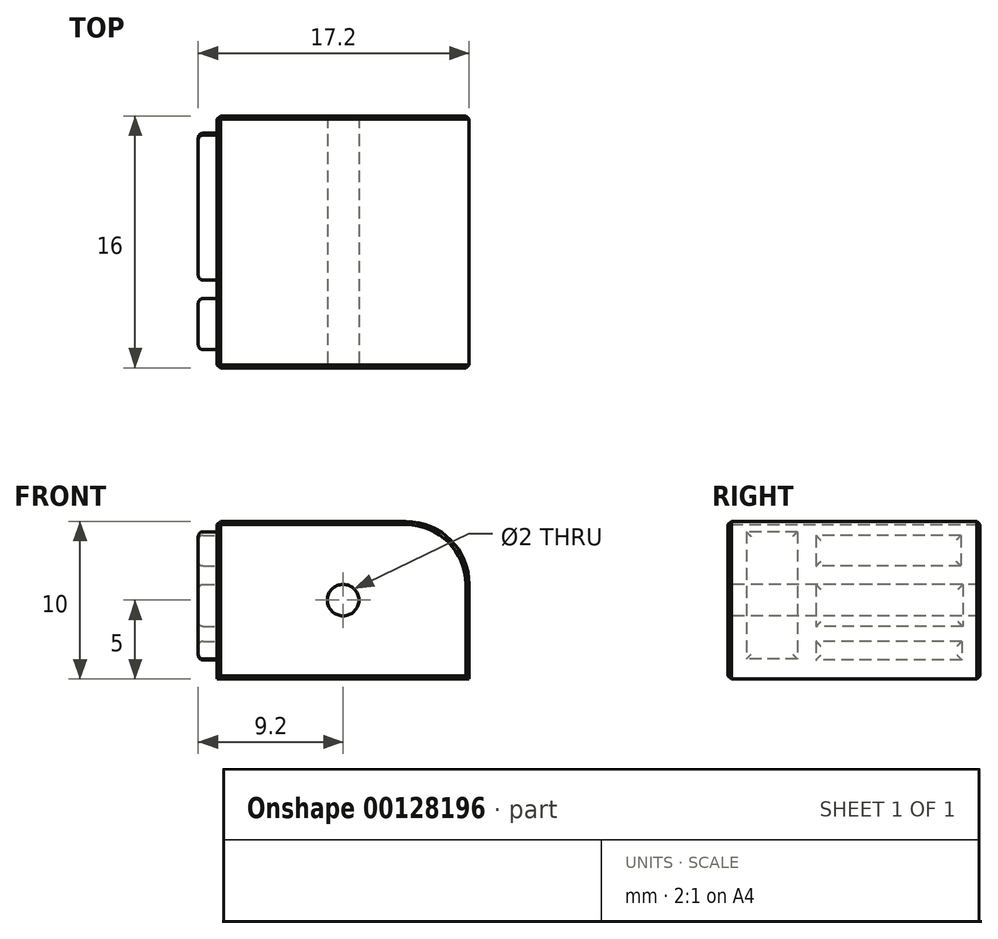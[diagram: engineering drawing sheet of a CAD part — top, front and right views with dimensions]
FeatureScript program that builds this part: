
annotation { "Feature Type Name" : "Feature", "Feature Type Description" : "" }
export const myFeature = defineFeature(function(context is Context, id is Id, definition is map)
    precondition{}
    {
        {
            var Q0;
            Q0=qCreatedBy(makeId("Top.planeOp"),FACE);
            var sketch = newSketch(context, id + "F0", { "sketchPlane" : qUnion([Q0])});
            skLineSegment(sketch, "E0.bottom", {"start": v(8, -8) * mm, "end": v(-8, -8) * mm});
            skLineSegment(sketch, "E0.top", {"start": v(8, 8) * mm, "end": v(-8, 8) * mm});
            skLineSegment(sketch, "E0.left", {"start": v(8, -8) * mm, "end": v(8, 8) * mm});
            skLineSegment(sketch, "E0.right", {"start": v(-8, -8) * mm, "end": v(-8, 8) * mm});
            skPoint(sketch, "E0.middle", {"position": v(0, 0) * mm});
            skSolve(sketch);
        }
        {
            var Q0;
            Q0=makeQuery(id+"F0.imprint","IMPRINT",FACE,{"disambiguationData":[TD([[makeQuery(id+"F0.imprint","IMPRINT",EDGE,{"derivedFrom":sQuery(id+"F0.wireOp",EDGE,"E0.bottom")}),-1.0]])]});
            extrude(context, id + "F1", {"entities" : qUnion([Q0]), "depth" : 10 * mm});
        }
        {
            var Q0;
            Q0=makeQuery(id+"F1.opExtrude","CAP_EDGE",EDGE,{"disambiguationData":[OSD([sQuery(id+"F0.wireOp",EDGE,"E0.left")])],"isStart":false});
            fillet(context, id + "F2", {"entities" : qUnion([Q0]), "radius" : 4 * mm, "tangentPropagation" : true, "allowEdgeOverflow" : false});
        }
        {
            var Q0;
            Q0=makeQuery(id+"F1.opExtrude","SWEPT_FACE",FACE,{"disambiguationData":[OSD([sQuery(id+"F0.wireOp",EDGE,"E0.right")])]});
            var sketch = newSketch(context, id + "F3", { "sketchPlane" : qUnion([Q0])});
            skLineSegment(sketch, "E1.bottom", {"start": v(-6.79, 9.1) * mm, "end": v(2.41, 9.1) * mm});
            skLineSegment(sketch, "E1.top", {"start": v(-6.79, 7.16) * mm, "end": v(2.41, 7.16) * mm});
            skLineSegment(sketch, "E1.left", {"start": v(-6.79, 9.1) * mm, "end": v(-6.79, 7.16) * mm});
            skLineSegment(sketch, "E1.right", {"start": v(2.41, 9.1) * mm, "end": v(2.41, 7.16) * mm});
            skLineSegment(sketch, "E2.bottom", {"start": v(-6.9, 5.98) * mm, "end": v(2.41, 5.98) * mm});
            skLineSegment(sketch, "E2.top", {"start": v(-6.9, 3.33) * mm, "end": v(2.41, 3.33) * mm});
            skLineSegment(sketch, "E2.left", {"start": v(-6.9, 5.98) * mm, "end": v(-6.9, 3.33) * mm});
            skLineSegment(sketch, "E2.right", {"start": v(2.41, 5.98) * mm, "end": v(2.41, 3.33) * mm});
            skLineSegment(sketch, "E3.bottom", {"start": v(-6.85, 2.38) * mm, "end": v(2.41, 2.38) * mm});
            skLineSegment(sketch, "E3.top", {"start": v(-6.85, 1.2) * mm, "end": v(2.41, 1.2) * mm});
            skLineSegment(sketch, "E3.left", {"start": v(-6.85, 2.38) * mm, "end": v(-6.85, 1.2) * mm});
            skLineSegment(sketch, "E3.right", {"start": v(2.41, 2.38) * mm, "end": v(2.41, 1.2) * mm});
            skLineSegment(sketch, "E4.bottom", {"start": v(3.6, 9.35) * mm, "end": v(6.84, 9.35) * mm});
            skLineSegment(sketch, "E4.top", {"start": v(3.6, 1.26) * mm, "end": v(6.84, 1.26) * mm});
            skLineSegment(sketch, "E4.left", {"start": v(3.6, 9.35) * mm, "end": v(3.6, 1.26) * mm});
            skLineSegment(sketch, "E4.right", {"start": v(6.84, 9.35) * mm, "end": v(6.84, 1.26) * mm});
            skSolve(sketch);
        }
        {
            var Q0;
            Q0=makeQuery(id+"F3.imprint","IMPRINT",FACE,{"disambiguationData":[TD([[makeQuery(id+"F3.imprint","IMPRINT",EDGE,{"derivedFrom":sQuery(id+"F3.wireOp",EDGE,"E1.bottom")}),-1.0]])]});
            var Q1;
            Q1=makeQuery(id+"F3.imprint","IMPRINT",FACE,{"disambiguationData":[TD([[makeQuery(id+"F3.imprint","IMPRINT",EDGE,{"derivedFrom":sQuery(id+"F3.wireOp",EDGE,"E2.bottom")}),-1.0]])]});
            var Q2;
            Q2=makeQuery(id+"F3.imprint","IMPRINT",FACE,{"disambiguationData":[TD([[makeQuery(id+"F3.imprint","IMPRINT",EDGE,{"derivedFrom":sQuery(id+"F3.wireOp",EDGE,"E3.bottom")}),-1.0]])]});
            var Q3;
            Q3=makeQuery(id+"F3.imprint","IMPRINT",FACE,{"disambiguationData":[TD([[makeQuery(id+"F3.imprint","IMPRINT",EDGE,{"derivedFrom":sQuery(id+"F3.wireOp",EDGE,"E4.bottom")}),-1.0]])]});
            extrude(context, id + "F4", {"entities" : qUnion([Q0, Q1, Q2, Q3]), "operationType" : NewBodyOperationType.ADD, "depth" : 1.2 * mm});
        }
        {
            var Q0;
            Q0=makeQuery(id+"F4.opExtrude","CAP_EDGE",EDGE,{"disambiguationData":[OSD([sQuery(id+"F3.wireOp",EDGE,"E1.bottom")])],"isStart":false});
            var Q1;
            Q1=makeQuery(id+"F4.opExtrude","CAP_EDGE",EDGE,{"disambiguationData":[OSD([sQuery(id+"F3.wireOp",EDGE,"E1.right")])],"isStart":false});
            var Q2;
            Q2=makeQuery(id+"F4.opExtrude","CAP_EDGE",EDGE,{"disambiguationData":[OSD([sQuery(id+"F3.wireOp",EDGE,"E1.top")])],"isStart":false});
            var Q3;
            Q3=makeQuery(id+"F4.opExtrude","CAP_EDGE",EDGE,{"disambiguationData":[OSD([sQuery(id+"F3.wireOp",EDGE,"E2.bottom")])],"isStart":false});
            var Q4;
            Q4=makeQuery(id+"F4.opExtrude","CAP_EDGE",EDGE,{"disambiguationData":[OSD([sQuery(id+"F3.wireOp",EDGE,"E2.right")])],"isStart":false});
            var Q5;
            Q5=makeQuery(id+"F4.opExtrude","CAP_EDGE",EDGE,{"disambiguationData":[OSD([sQuery(id+"F3.wireOp",EDGE,"E2.top")])],"isStart":false});
            var Q6;
            Q6=makeQuery(id+"F4.opExtrude","CAP_EDGE",EDGE,{"disambiguationData":[OSD([sQuery(id+"F3.wireOp",EDGE,"E3.bottom")])],"isStart":false});
            var Q7;
            Q7=makeQuery(id+"F4.opExtrude","CAP_EDGE",EDGE,{"disambiguationData":[OSD([sQuery(id+"F3.wireOp",EDGE,"E3.right")])],"isStart":false});
            var Q8;
            Q8=makeQuery(id+"F4.opExtrude","CAP_EDGE",EDGE,{"disambiguationData":[OSD([sQuery(id+"F3.wireOp",EDGE,"E3.top")])],"isStart":false});
            var Q9;
            Q9=makeQuery(id+"F4.opExtrude","CAP_EDGE",EDGE,{"disambiguationData":[OSD([sQuery(id+"F3.wireOp",EDGE,"E4.bottom")])],"isStart":false});
            var Q10;
            Q10=makeQuery(id+"F4.opExtrude","CAP_EDGE",EDGE,{"disambiguationData":[OSD([sQuery(id+"F3.wireOp",EDGE,"E4.right")])],"isStart":false});
            var Q11;
            Q11=makeQuery(id+"F4.opExtrude","CAP_EDGE",EDGE,{"disambiguationData":[OSD([sQuery(id+"F3.wireOp",EDGE,"E4.left")])],"isStart":false});
            var Q12;
            Q12=makeQuery(id+"F4.opExtrude","CAP_EDGE",EDGE,{"disambiguationData":[OSD([sQuery(id+"F3.wireOp",EDGE,"E4.top")])],"isStart":false});
            var Q13;
            Q13=makeQuery(id+"F4.opExtrude","CAP_EDGE",EDGE,{"disambiguationData":[OSD([sQuery(id+"F3.wireOp",EDGE,"E1.left")])],"isStart":false});
            var Q14;
            Q14=makeQuery(id+"F4.opExtrude","CAP_EDGE",EDGE,{"disambiguationData":[OSD([sQuery(id+"F3.wireOp",EDGE,"E2.left")])],"isStart":false});
            var Q15;
            Q15=makeQuery(id+"F4.opExtrude","CAP_EDGE",EDGE,{"disambiguationData":[OSD([sQuery(id+"F3.wireOp",EDGE,"E3.left")])],"isStart":false});
            fillet(context, id + "F5", {"entities" : qUnion([Q0, Q1, Q2, Q3, Q4, Q5, Q6, Q7, Q8, Q9, Q10, Q11, Q12, Q13, Q14, Q15]), "radius" : .3 * mm, "tangentPropagation" : true, "allowEdgeOverflow" : false});
        }
        {
            var Q0;
            Q0=makeQuery(id+"F1.opExtrude","SWEPT_FACE",FACE,{"disambiguationData":[OSD([sQuery(id+"F0.wireOp",EDGE,"E0.bottom")])]});
            var Q1;
            Q1=makeQuery(id+"F1.opExtrude","SWEPT_FACE",FACE,{"disambiguationData":[OSD([sQuery(id+"F0.wireOp",EDGE,"E0.top")])]});
            var Q2;
            Q2=makeQuery(id+"F1.opExtrude","CAP_EDGE",EDGE,{"disambiguationData":[OSD([sQuery(id+"F0.wireOp",EDGE,"E0.right")])],"isStart":false});
            chamfer(context, id + "F6", {"entities" : qUnion([Q0, Q1, Q2]), "width" : .2 * mm, "tangentPropagation" : true});
        }
        {
            var Q0;
            Q0=makeQuery(id+"F1.opExtrude","SWEPT_FACE",FACE,{"disambiguationData":[OSD([sQuery(id+"F0.wireOp",EDGE,"E0.bottom")])]});
            var sketch = newSketch(context, id + "F7", { "sketchPlane" : qUnion([Q0])});
            skCircle(sketch, "E5", {"center": v(0, 5) * mm, "radius": 1 * mm});
            skPoint(sketch, "E5.centerSnap0", {"position": v(-7.8, 5) * mm});
            skSolve(sketch);
        }
        {
            var Q0;
            Q0=makeQuery(id+"F7.imprint","IMPRINT",FACE,{"disambiguationData":[TD([[makeQuery(id+"F7.imprint","IMPRINT",EDGE,{"derivedFrom":sQuery(id+"F7.wireOp",EDGE,"E5")}),1.0]])]});
            extrude(context, id + "F8", {"entities" : qUnion([Q0]), "operationType" : NewBodyOperationType.REMOVE, "endBound" : BoundingType.THROUGH_ALL, "oppositeDirection" : true, "depth" : 25 * mm});
        }
    });
